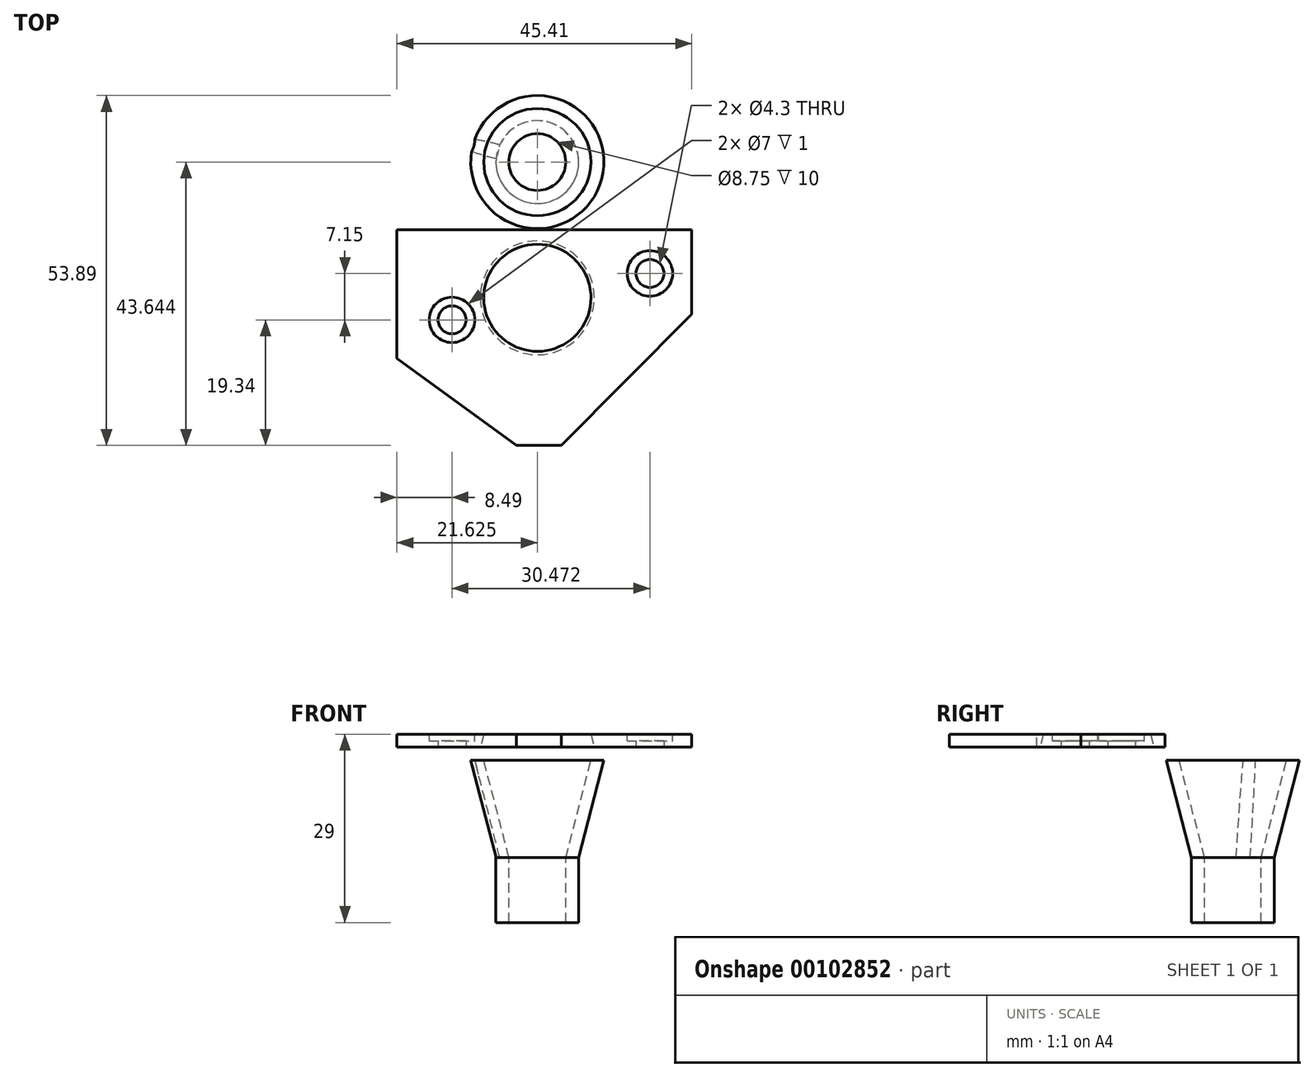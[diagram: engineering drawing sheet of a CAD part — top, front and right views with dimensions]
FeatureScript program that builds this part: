
annotation { "Feature Type Name" : "Feature", "Feature Type Description" : "" }
export const myFeature = defineFeature(function(context is Context, id is Id, definition is map)
    precondition{}
    {
        {
            var Q0;
            Q0=qCreatedBy(makeId("Top.planeOp"),FACE);
            var sketch = newSketch(context, id + "F0", { "sketchPlane" : qUnion([Q0])});
            skCircle(sketch, "E0", {"center": v(30.47, -7.15) * mm, "radius": 2.15 * mm});
            skCircle(sketch, "E1", {"center": v(0, 0) * mm, "radius": 2.15 * mm});
            skLineSegment(sketch, "E2.bottom", {"start": v(18.9, -9.35) * mm, "end": v(7.4, -9.35) * mm});
            skLineSegment(sketch, "E2.top", {"start": v(18.89, 10.65) * mm, "end": v(7.39, 10.65) * mm});
            skLineSegment(sketch, "E2.left", {"start": v(18.9, -9.35) * mm, "end": v(18.89, 10.65) * mm});
            skLineSegment(sketch, "E2.right", {"start": v(7.4, -9.35) * mm, "end": v(7.39, 10.65) * mm});
            skLineSegment(sketch, "E3.bottom", {"start": v(36.92, -13.85) * mm, "end": v(-8.49, -13.85) * mm});
            skLineSegment(sketch, "E3.top", {"start": v(36.92, 19.34) * mm, "end": v(-8.49, 19.34) * mm});
            skLineSegment(sketch, "E3.left", {"start": v(36.92, -13.85) * mm, "end": v(36.92, 19.34) * mm});
            skLineSegment(sketch, "E3.right", {"start": v(-8.49, -13.85) * mm, "end": v(-8.49, 19.34) * mm});
            skLineSegment(sketch, "E4", {"start": v(18.9, 2.15) * mm, "end": v(7.39, 2.15) * mm});
            skSolve(sketch);
        }
        {
            var Q0;
            Q0=makeQuery(id+"F0.imprint","IMPRINT",FACE,{"disambiguationData":[TD([[makeQuery(id+"F0.imprint","IMPRINT",EDGE,{"derivedFrom":sQuery(id+"F0.wireOp",EDGE,"E0")}),-1.0]])]});
            var Q1;
            Q1=makeQuery(id+"F0.imprint","IMPRINT",FACE,{"disambiguationData":[TD([[makeQuery(id+"F0.imprint","IMPRINT",EDGE,{"derivedFrom":sQuery(id+"F0.wireOp",EDGE,"E2.bottom")}),1.0]])]});
            var Q2;
            {var subQ0=sQuery(id+"F0.wireOp",EDGE,"E2.top");Q2=makeQuery(id+"F0.imprint","IMPRINT",FACE,{"disambiguationData":[TD([[makeQuery(id+"F0.imprint","IMPRINT",EDGE,{"derivedFrom":subQ0}),1.0]])]});}
            extrude(context, id + "F1", {"entities" : qUnion([Q0, Q1, Q2]), "oppositeDirection" : true, "depth" : 2 * mm});
        }
        {
            var Q0;
            Q0=makeQuery(id+"F1.opExtrude","CAP_FACE",FACE,{"disambiguationData":[OSD([sQuery(id+"F0.wireOp",EDGE,"E0"),sQuery(id+"F0.wireOp",EDGE,"E1"),sQuery(id+"F0.wireOp",EDGE,"E2.bottom"),sQuery(id+"F0.wireOp",EDGE,"E2.top"),sQuery(id+"F0.wireOp",EDGE,"E2.left"),sQuery(id+"F0.wireOp",EDGE,"E2.right"),sQuery(id+"F0.wireOp",EDGE,"E3.bottom"),sQuery(id+"F0.wireOp",EDGE,"E3.top"),sQuery(id+"F0.wireOp",EDGE,"E3.left"),sQuery(id+"F0.wireOp",EDGE,"E3.right")])],"isStart":false});
            var sketch = newSketch(context, id + "F2", { "sketchPlane" : qUnion([Q0])});
            skCircle(sketch, "E5", {"center": v(0, 0) * mm, "radius": 3.5 * mm});
            skCircle(sketch, "E6", {"center": v(30.47, 7.15) * mm, "radius": 3.5 * mm});
            skSolve(sketch);
        }
        {
            var Q0;
            Q0=makeQuery(id+"F2.imprint","IMPRINT",FACE,{"disambiguationData":[TD([[makeQuery(id+"F2.imprint","IMPRINT",EDGE,{"derivedFrom":sQuery(id+"F2.wireOp",EDGE,"E6")}),1.0]])]});
            var Q1;
            Q1=makeQuery(id+"F2.imprint","IMPRINT",FACE,{"disambiguationData":[TD([[makeQuery(id+"F2.imprint","IMPRINT",EDGE,{"derivedFrom":sQuery(id+"F2.wireOp",EDGE,"E5")}),1.0]])]});
            extrude(context, id + "F3", {"entities" : qUnion([Q0, Q1]), "operationType" : NewBodyOperationType.REMOVE, "oppositeDirection" : true, "depth" : 1 * mm});
        }
        {
            var Q0;
            Q0=makeQuery(id+"F1.opExtrude","CAP_FACE",FACE,{"disambiguationData":[OSD([sQuery(id+"F0.wireOp",EDGE,"E0"),sQuery(id+"F0.wireOp",EDGE,"E1"),sQuery(id+"F0.wireOp",EDGE,"E2.bottom"),sQuery(id+"F0.wireOp",EDGE,"E2.top"),sQuery(id+"F0.wireOp",EDGE,"E2.left"),sQuery(id+"F0.wireOp",EDGE,"E2.right"),sQuery(id+"F0.wireOp",EDGE,"E3.bottom"),sQuery(id+"F0.wireOp",EDGE,"E3.top"),sQuery(id+"F0.wireOp",EDGE,"E3.left"),sQuery(id+"F0.wireOp",EDGE,"E3.right")])],"isStart":false});
            var sketch = newSketch(context, id + "F4", { "sketchPlane" : qUnion([Q0])});
            skCircle(sketch, "E7", {"center": v(13.14, 3.4) * mm, "radius": 8.25 * mm});
            skCircle(sketch, "E8", {"center": v(13.14, 3.4) * mm, "radius": 10.25 * mm});
            skSolve(sketch);
        }
        {
            var Q0;
            Q0=makeQuery(id+"F4.imprint","IMPRINT",FACE,{"disambiguationData":[TD([[makeQuery(id+"F4.imprint","IMPRINT",EDGE,{"derivedFrom":sQuery(id+"F4.wireOp",EDGE,"E8")}),-1.0]])]});
            var Q1;
            Q1=qBodyType(qCreatedBy(id+"F6",EDGE),BodyType.WIRE);
            cPlane(context, id + "F5", {"entities" : qUnion([Q0, Q1]), "cplaneType" : CPlaneType.OFFSET, "offset" : 15 * mm, "width" : 150 * mm, "height" : 150 * mm});
        }
        {
            var Q0;
            Q0=qCreatedBy(id+"F5.planeOp",FACE);
            var sketch = newSketch(context, id + "F6", { "sketchPlane" : qUnion([Q0])});
            skCircle(sketch, "E9", {"center": v(13.14, 3.4) * mm, "radius": 6.37 * mm});
            skCircle(sketch, "E10", {"center": v(13.14, 3.4) * mm, "radius": 4.38 * mm});
            skSolve(sketch);
        }
        {
            var Q0;
            Q0=makeQuery(id+"F6.imprint","IMPRINT",FACE,{"disambiguationData":[TD([[makeQuery(id+"F6.imprint","IMPRINT",EDGE,{"derivedFrom":sQuery(id+"F6.wireOp",EDGE,"E9")}),1.0]])]});
            extrude(context, id + "F7", {"entities" : qUnion([Q0]), "depth" : 10 * mm});
        }
        {
            var Q0;
            Q0=makeQuery(id+"F4.imprint","IMPRINT",FACE,{"disambiguationData":[TD([[makeQuery(id+"F4.imprint","IMPRINT",EDGE,{"derivedFrom":makeQuery(id+"F1.opExtrude","CAP_EDGE",EDGE,{"disambiguationData":[OSD([sQuery(id+"F0.wireOp",EDGE,"E2.bottom")])],"isStart":false})}),1.0]])]});
            var Q1;
            Q1=makeQuery(id+"F4.imprint","IMPRINT",FACE,{"disambiguationData":[TD([[makeQuery(id+"F4.imprint","IMPRINT",EDGE,{"derivedFrom":sQuery(id+"F4.wireOp",EDGE,"E7")}),1.0]])]});
            var Q2;
            Q2=makeQuery(id+"F4.imprint","IMPRINT",FACE,{"disambiguationData":[TD([[makeQuery(id+"F4.imprint","IMPRINT",EDGE,{"derivedFrom":sQuery(id+"F4.wireOp",EDGE,"E7")}),-1.0]])]});
            var Q3;
            {var subQ0=sQuery(id+"F4.wireOp",EDGE,"E7");var subQ1=makeQuery(id+"F1.opExtrude","CAP_EDGE",EDGE,{"disambiguationData":[OSD([sQuery(id+"F0.wireOp",EDGE,"E2.right")])],"isStart":false});var subQ2=makeQuery(id+"F4.imprint","INTERSECT",VERTEX,{"disambiguationData":[OD(1.0)],"derivedFrom":[subQ1,subQ0]});Q3=makeQuery(id+"F4.imprint","IMPRINT",FACE,{"disambiguationData":[TD([[makeQuery(id+"F4.imprint","IMPRINT",EDGE,{"disambiguationData":[TD([[subQ2,-1.0]])],"derivedFrom":subQ0}),-1.0]])]});}
            var Q4;
            {var subQ0=sQuery(id+"F4.wireOp",EDGE,"E7");var subQ1=makeQuery(id+"F1.opExtrude","CAP_EDGE",EDGE,{"disambiguationData":[OSD([sQuery(id+"F0.wireOp",EDGE,"E2.bottom")])],"isStart":false});var subQ2=makeQuery(id+"F4.imprint","INTERSECT",VERTEX,{"disambiguationData":[OD(0.0)],"derivedFrom":[subQ1,subQ0]});Q4=makeQuery(id+"F4.imprint","IMPRINT",FACE,{"disambiguationData":[TD([[makeQuery(id+"F4.imprint","IMPRINT",EDGE,{"disambiguationData":[TD([[subQ2,-1.0]])],"derivedFrom":subQ0}),1.0]])]});}
            var Q5;
            {var subQ0=sQuery(id+"F4.wireOp",EDGE,"E7");var subQ1=makeQuery(id+"F1.opExtrude","CAP_EDGE",EDGE,{"disambiguationData":[OSD([sQuery(id+"F0.wireOp",EDGE,"E2.left")])],"isStart":false});var subQ2=makeQuery(id+"F4.imprint","INTERSECT",VERTEX,{"disambiguationData":[OD(0.0)],"derivedFrom":[subQ1,subQ0]});Q5=makeQuery(id+"F4.imprint","IMPRINT",FACE,{"disambiguationData":[TD([[makeQuery(id+"F4.imprint","IMPRINT",EDGE,{"disambiguationData":[TD([[subQ2,1.0]])],"derivedFrom":subQ0}),1.0]])]});}
            var Q6;
            {var subQ0=sQuery(id+"F4.wireOp",EDGE,"E7");var subQ1=makeQuery(id+"F1.opExtrude","CAP_EDGE",EDGE,{"disambiguationData":[OSD([sQuery(id+"F0.wireOp",EDGE,"E2.right")])],"isStart":false});var subQ2=makeQuery(id+"F4.imprint","INTERSECT",VERTEX,{"disambiguationData":[OD(0.0)],"derivedFrom":[subQ1,subQ0]});Q6=makeQuery(id+"F4.imprint","IMPRINT",FACE,{"disambiguationData":[TD([[makeQuery(id+"F4.imprint","IMPRINT",EDGE,{"disambiguationData":[TD([[subQ2,-1.0]])],"derivedFrom":subQ0}),1.0]])]});}
            extrude(context, id + "F8", {"entities" : qUnion([Q0, Q1, Q2, Q3, Q4, Q5, Q6]), "depth" : 15 * mm, "hasDraft" : true, "draftAngle" : 14.5 * degree, "draftPullDirection" : true});
        }
        {
            var Q0;
            Q0=makeQuery(id+"F6.imprint","IMPRINT",FACE,{"disambiguationData":[TD([[makeQuery(id+"F6.imprint","IMPRINT",EDGE,{"derivedFrom":sQuery(id+"F6.wireOp",EDGE,"E10")}),1.0]])]});
            var Q1;
            Q1=makeQuery(id+"F1.opExtrude","CAP_FACE",FACE,{"disambiguationData":[OSD([sQuery(id+"F0.wireOp",EDGE,"E0"),sQuery(id+"F0.wireOp",EDGE,"E1"),sQuery(id+"F0.wireOp",EDGE,"E2.bottom"),sQuery(id+"F0.wireOp",EDGE,"E2.top"),sQuery(id+"F0.wireOp",EDGE,"E2.left"),sQuery(id+"F0.wireOp",EDGE,"E2.right"),sQuery(id+"F0.wireOp",EDGE,"E3.bottom"),sQuery(id+"F0.wireOp",EDGE,"E3.top"),sQuery(id+"F0.wireOp",EDGE,"E3.left"),sQuery(id+"F0.wireOp",EDGE,"E3.right")])],"isStart":true});
            extrude(context, id + "F9", {"entities" : qUnion([Q0]), "operationType" : NewBodyOperationType.REMOVE, "endBound" : BoundingType.UP_TO_SURFACE, "oppositeDirection" : true, "endBoundEntityFace" : qUnion([Q1]), "depth" : 25 * mm, "hasDraft" : true, "draftAngle" : 14.5 * degree});
        }
        {
            var Q0;
            Q0=makeQuery(id+"F1.opExtrude","CAP_FACE",FACE,{"disambiguationData":[OSD([sQuery(id+"F0.wireOp",EDGE,"E0"),sQuery(id+"F0.wireOp",EDGE,"E1"),sQuery(id+"F0.wireOp",EDGE,"E2.bottom"),sQuery(id+"F0.wireOp",EDGE,"E2.top"),sQuery(id+"F0.wireOp",EDGE,"E2.left"),sQuery(id+"F0.wireOp",EDGE,"E2.right"),sQuery(id+"F0.wireOp",EDGE,"E3.bottom"),sQuery(id+"F0.wireOp",EDGE,"E3.top"),sQuery(id+"F0.wireOp",EDGE,"E3.left"),sQuery(id+"F0.wireOp",EDGE,"E3.right")])],"isStart":false});
            var sketch = newSketch(context, id + "F10", { "sketchPlane" : qUnion([Q0])});
            skLineSegment(sketch, "E11", {"start": v(9.9, -19.34) * mm, "end": v(-8.49, -5.92) * mm});
            skLineSegment(sketch, "E12", {"start": v(-8.49, -5.92) * mm, "end": v(-8.49, -19.34) * mm});
            skLineSegment(sketch, "E13", {"start": v(-8.49, -19.34) * mm, "end": v(9.9, -19.34) * mm});
            skLineSegment(sketch, "E14", {"start": v(16.84, -19.34) * mm, "end": v(36.92, 0.88) * mm});
            skLineSegment(sketch, "E15", {"start": v(36.92, 0.88) * mm, "end": v(36.92, -19.34) * mm});
            skLineSegment(sketch, "E16", {"start": v(36.92, -19.34) * mm, "end": v(16.84, -19.34) * mm});
            skSolve(sketch);
        }
        {
            var Q0;
            Q0=makeQuery(id+"F10.imprint","IMPRINT",FACE,{"disambiguationData":[TD([[makeQuery(id+"F10.imprint","IMPRINT",EDGE,{"derivedFrom":sQuery(id+"F10.wireOp",EDGE,"h9qNYmhN-c2CS-bT2P-m7KC-hRlkTBGNkaa8")}),1.0]])]});
            var Q1;
            Q1=makeQuery(id+"F10.imprint","IMPRINT",FACE,{"disambiguationData":[TD([[makeQuery(id+"F10.imprint","IMPRINT",EDGE,{"derivedFrom":sQuery(id+"F10.wireOp",EDGE,"E14")}),-1.0]])]});
            var Q2;
            Q2=makeQuery(id+"F10.imprint","IMPRINT",FACE,{"disambiguationData":[TD([[makeQuery(id+"F10.imprint","IMPRINT",EDGE,{"derivedFrom":sQuery(id+"F10.wireOp",EDGE,"E11")}),1.0]])]});
            extrude(context, id + "F11", {"entities" : qUnion([Q0, Q1, Q2]), "operationType" : NewBodyOperationType.REMOVE, "endBound" : BoundingType.UP_TO_NEXT, "oppositeDirection" : true, "depth" : 25 * mm});
        }
        {
            var Q0;
            Q0=makeQuery(id+"F1.opExtrude","SWEPT_BODY",BODY,{"disambiguationData":[OSD([sQuery(id+"F0.wireOp",EDGE,"E0"),sQuery(id+"F0.wireOp",EDGE,"E1"),sQuery(id+"F0.wireOp",EDGE,"E2.bottom"),sQuery(id+"F0.wireOp",EDGE,"E2.top"),sQuery(id+"F0.wireOp",EDGE,"E2.left"),sQuery(id+"F0.wireOp",EDGE,"E2.right"),sQuery(id+"F0.wireOp",EDGE,"E3.bottom"),sQuery(id+"F0.wireOp",EDGE,"E3.top"),sQuery(id+"F0.wireOp",EDGE,"E3.left"),sQuery(id+"F0.wireOp",EDGE,"E3.right")])]});
            var Q1;
            Q1=makeQuery(id+"F1.opExtrude","CAP_EDGE",EDGE,{"disambiguationData":[OSD([sQuery(id+"F0.wireOp",EDGE,"E3.bottom")])],"isStart":true});
            transform(context, id + "F12", {"entities" : qUnion([Q0]), "transformType" : TransformType.ROTATION, "transformAxis" : qUnion([Q1]), "angle" : 180 * degree, "makeCopy" : false});
        }
    });
